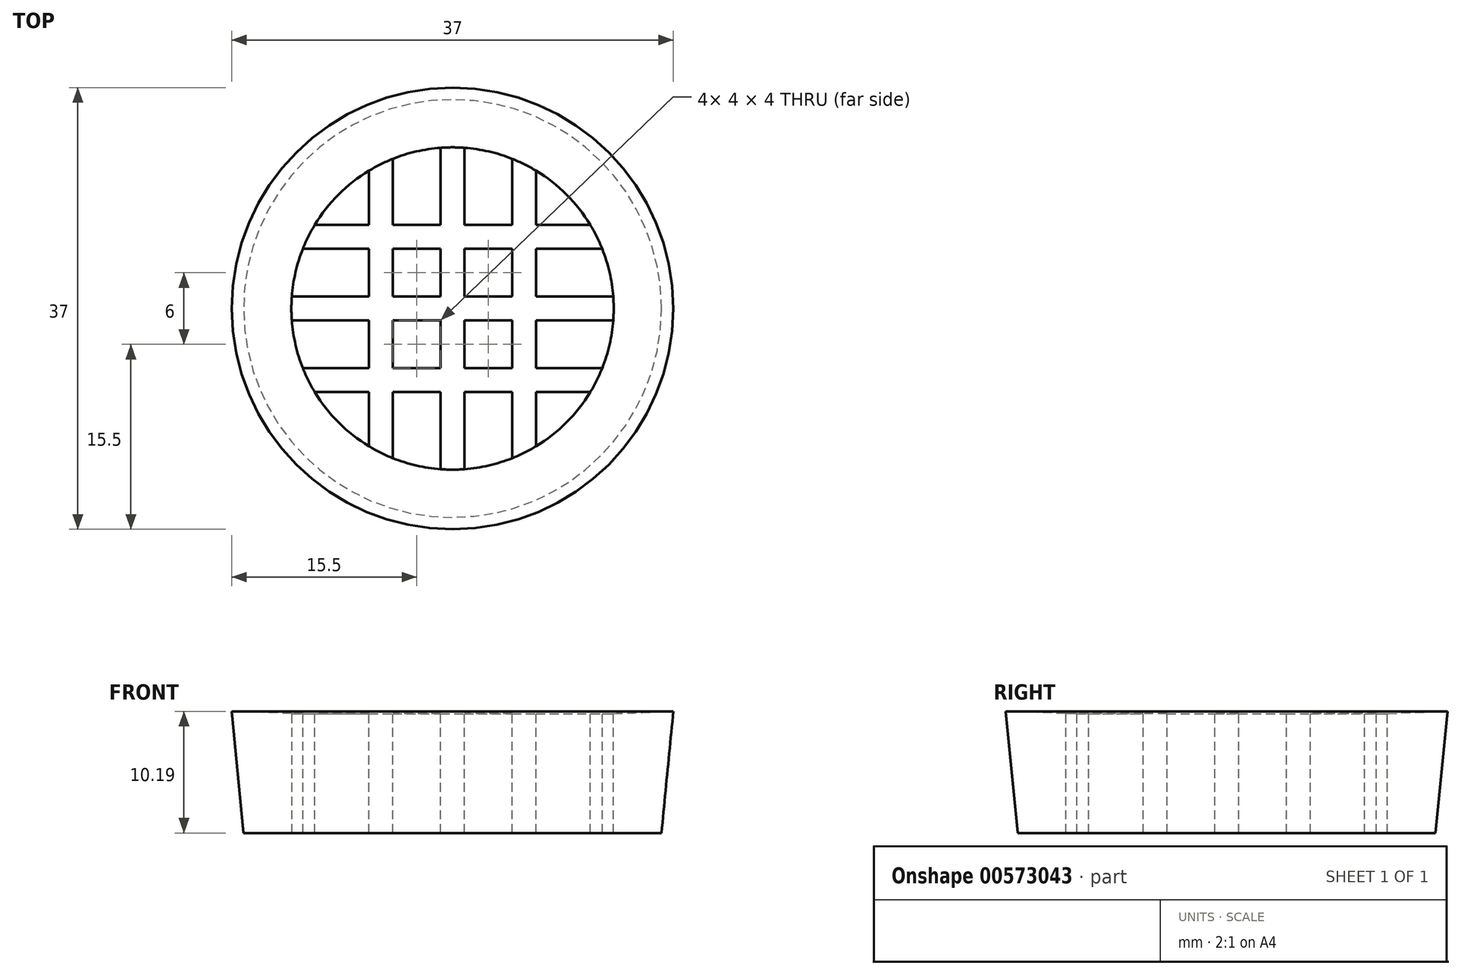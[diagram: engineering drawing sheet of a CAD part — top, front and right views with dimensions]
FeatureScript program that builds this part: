
annotation { "Feature Type Name" : "Feature", "Feature Type Description" : "" }
export const myFeature = defineFeature(function(context is Context, id is Id, definition is map)
    precondition{}
    {
        {
            var Q0;
            Q0=qCreatedBy(makeId("Front.planeOp"),FACE);
            var sketch = newSketch(context, id + "F0", { "sketchPlane" : qUnion([Q0])});
            skLineSegment(sketch, "E0", {"start": v(0, 68.06) * mm, "end": v(0, -62.01) * mm, "construction": true});
            skLineSegment(sketch, "E1", {"start": v(-17.5, 0) * mm, "end": v(-18.5, 10.2) * mm});
            skLineSegment(sketch, "E2", {"start": v(-18.5, 10.2) * mm, "end": v(-13.5, 10) * mm});
            skLineSegment(sketch, "E3", {"start": v(-13.5, 10) * mm, "end": v(-13.5, 0) * mm});
            skLineSegment(sketch, "E4", {"start": v(-13.5, 0) * mm, "end": v(-17.5, 0) * mm});
            skSolve(sketch);
        }
        {
            var Q0;
            Q0=makeQuery(id+"F0.imprint","IMPRINT",FACE,{"disambiguationData":[TD([[makeQuery(id+"F0.imprint","IMPRINT",EDGE,{"derivedFrom":sQuery(id+"F0.wireOp",EDGE,"E1")}),-1.0]])]});
            var Q1;
            Q1=sQuery(id+"F0.wireOp",EDGE,"E0");
            revolve(context, id + "F1", {"surfaceOperationType" : NewSurfaceOperationType.NEW, "entities" : qUnion([Q0]), "axis" : qUnion([Q1]), "revolveType" : RevolveType.FULL});
        }
        {
            var Q0;
            Q0=qCreatedBy(makeId("Top.planeOp"),FACE);
            var sketch = newSketch(context, id + "F2", { "sketchPlane" : qUnion([Q0])});
            skArc(sketch, "E5", {"start": v(-11.67, 7) * mm, "mid": v(-12.2, 6.02) * mm, "end": v(-12.65, 5) * mm});
            skLineSegment(sketch, "E6", {"start": v(-13.57, 1) * mm, "end": v(-7, 1) * mm});
            skLineSegment(sketch, "E7", {"start": v(-13.57, -1) * mm, "end": v(-7, -1) * mm});
            skLineSegment(sketch, "E8", {"start": v(-12.65, 5) * mm, "end": v(-7, 5) * mm});
            skLineSegment(sketch, "E9", {"start": v(-11.67, 7) * mm, "end": v(-7, 7) * mm});
            skLineSegment(sketch, "E10", {"start": v(-12.65, -5) * mm, "end": v(-7, -5) * mm});
            skLineSegment(sketch, "E11", {"start": v(-11.67, -7) * mm, "end": v(-7, -7) * mm});
            skLineSegment(sketch, "E12", {"start": v(15.82, 0) * mm, "end": v(13.6, 0) * mm, "construction": true});
            skLineSegment(sketch, "E13", {"start": v(-1, 13.57) * mm, "end": v(-1, 7) * mm});
            skLineSegment(sketch, "E14", {"start": v(1, -13.57) * mm, "end": v(1, -7) * mm});
            skLineSegment(sketch, "E15", {"start": v(5, 12.65) * mm, "end": v(5, 7) * mm});
            skLineSegment(sketch, "E16", {"start": v(7, -11.67) * mm, "end": v(7, -7) * mm});
            skLineSegment(sketch, "E17", {"start": v(-7, 11.67) * mm, "end": v(-7, 7) * mm});
            skLineSegment(sketch, "E18", {"start": v(-5, -12.65) * mm, "end": v(-5, -7) * mm});
            skLineSegment(sketch, "E19.trimOffspring", {"start": v(-5, 7) * mm, "end": v(-1, 7) * mm});
            skLineSegment(sketch, "E20.trimOffspring", {"start": v(-5, 5) * mm, "end": v(-1, 5) * mm});
            skLineSegment(sketch, "E21.trimOffspring", {"start": v(-7, 5) * mm, "end": v(-7, 1) * mm});
            skLineSegment(sketch, "E22.trimOffspring", {"start": v(-5, 7) * mm, "end": v(-5, 12.65) * mm});
            skLineSegment(sketch, "E23.trimOffspring", {"start": v(-1, 5) * mm, "end": v(-1, 1) * mm});
            skLineSegment(sketch, "E24.trimOffspring", {"start": v(1, 7) * mm, "end": v(5, 7) * mm});
            skLineSegment(sketch, "E25.trimOffspring", {"start": v(7, 7) * mm, "end": v(11.67, 7) * mm});
            skLineSegment(sketch, "E26.trimOffspring", {"start": v(1, 5) * mm, "end": v(5, 5) * mm});
            skLineSegment(sketch, "E27.trimOffspring", {"start": v(1, 1) * mm, "end": v(5, 1) * mm});
            skLineSegment(sketch, "E28.trimOffspring", {"start": v(1, -1) * mm, "end": v(5, -1) * mm});
            skLineSegment(sketch, "E29.trimOffspring", {"start": v(1, -5) * mm, "end": v(5, -5) * mm});
            skLineSegment(sketch, "E30.trimOffspring", {"start": v(1, -7) * mm, "end": v(5, -7) * mm});
            skLineSegment(sketch, "E31.trimOffspring", {"start": v(-1, -7) * mm, "end": v(-1, -13.57) * mm});
            skLineSegment(sketch, "E32.trimOffspring", {"start": v(1, -5) * mm, "end": v(1, -1) * mm});
            skLineSegment(sketch, "E33.trimOffspring", {"start": v(-5, -5) * mm, "end": v(-5, -1) * mm});
            skLineSegment(sketch, "E34.trimOffspring", {"start": v(-7, -7) * mm, "end": v(-7, -11.67) * mm});
            skLineSegment(sketch, "E35.trimOffspring", {"start": v(-5, -5) * mm, "end": v(-1, -5) * mm});
            skLineSegment(sketch, "E36.trimOffspring", {"start": v(-5, -7) * mm, "end": v(-1, -7) * mm});
            skLineSegment(sketch, "E37.trimOffspring", {"start": v(5, 5) * mm, "end": v(5, 1) * mm});
            skLineSegment(sketch, "E38.trimOffspring", {"start": v(7, 5) * mm, "end": v(12.65, 5) * mm});
            skLineSegment(sketch, "E39.trimOffspring", {"start": v(7, 7) * mm, "end": v(7, 11.67) * mm});
            skLineSegment(sketch, "E40.trimOffspring", {"start": v(1, 7) * mm, "end": v(1, 13.57) * mm});
            skLineSegment(sketch, "E41.trimOffspring", {"start": v(7, 1) * mm, "end": v(13.57, 1) * mm});
            skLineSegment(sketch, "E42.trimOffspring", {"start": v(7, 1) * mm, "end": v(7, 5) * mm});
            skLineSegment(sketch, "E43.trimOffspring", {"start": v(1, 0) * mm, "end": v(-1, 0) * mm, "construction": true});
            skLineSegment(sketch, "E44.trimOffspring", {"start": v(7, -1) * mm, "end": v(13.57, -1) * mm});
            skLineSegment(sketch, "E45.trimOffspring", {"start": v(5, -1) * mm, "end": v(5, -5) * mm});
            skLineSegment(sketch, "E46.trimOffspring", {"start": v(7, -5) * mm, "end": v(12.65, -5) * mm});
            skLineSegment(sketch, "E47.trimOffspring", {"start": v(7, -7) * mm, "end": v(11.67, -7) * mm});
            skLineSegment(sketch, "E48.trimOffspring", {"start": v(5, -7) * mm, "end": v(5, -12.65) * mm});
            skLineSegment(sketch, "E49.trimOffspring", {"start": v(7, -5) * mm, "end": v(7, -1) * mm});
            skLineSegment(sketch, "E50.trimOffspring", {"start": v(-5, 0) * mm, "end": v(-30.47, 0) * mm, "construction": true});
            skLineSegment(sketch, "E51.trimOffspring", {"start": v(-5, 1) * mm, "end": v(-5, 5) * mm});
            skLineSegment(sketch, "E52.trimOffspring", {"start": v(-5, -1) * mm, "end": v(-1, -1) * mm});
            skLineSegment(sketch, "E53.trimOffspring", {"start": v(-5, 1) * mm, "end": v(-1, 1) * mm});
            skLineSegment(sketch, "E54.trimOffspring", {"start": v(-7, -1) * mm, "end": v(-7, -5) * mm});
            skLineSegment(sketch, "E55.trimOffspring", {"start": v(-1, -1) * mm, "end": v(-1, -5) * mm});
            skLineSegment(sketch, "E56.trimOffspring", {"start": v(1, 1) * mm, "end": v(1, 5) * mm});
            skArc(sketch, "E57.trimOffspring", {"start": v(-5, 12.65) * mm, "mid": v(-6.02, 12.2) * mm, "end": v(-7, 11.67) * mm});
            skArc(sketch, "E58.trimOffspring", {"start": v(1, 13.57) * mm, "mid": v(0, 13.6) * mm, "end": v(-1, 13.57) * mm});
            skArc(sketch, "E59.trimOffspring", {"start": v(7, 11.67) * mm, "mid": v(6.02, 12.2) * mm, "end": v(5, 12.65) * mm});
            skArc(sketch, "E60.trimOffspring", {"start": v(12.65, 5) * mm, "mid": v(12.2, 6.02) * mm, "end": v(11.67, 7) * mm});
            skArc(sketch, "E61.trimOffspring", {"start": v(13.57, -1) * mm, "mid": v(13.6, 0) * mm, "end": v(13.57, 1) * mm});
            skArc(sketch, "E62.trimOffspring", {"start": v(11.67, -7) * mm, "mid": v(12.2, -6.02) * mm, "end": v(12.65, -5) * mm});
            skArc(sketch, "E63.trimOffspring", {"start": v(5, -12.65) * mm, "mid": v(6.02, -12.2) * mm, "end": v(7, -11.67) * mm});
            skArc(sketch, "E64.trimOffspring", {"start": v(-1, -13.57) * mm, "mid": v(0, -13.6) * mm, "end": v(1, -13.57) * mm});
            skArc(sketch, "E65.trimOffspring", {"start": v(-7, -11.67) * mm, "mid": v(-6.02, -12.2) * mm, "end": v(-5, -12.65) * mm});
            skArc(sketch, "E66.trimOffspring", {"start": v(-12.65, -5) * mm, "mid": v(-12.2, -6.02) * mm, "end": v(-11.67, -7) * mm});
            skArc(sketch, "E67.trimOffspring", {"start": v(-13.57, 1) * mm, "mid": v(-13.6, 0) * mm, "end": v(-13.57, -1) * mm});
            skSolve(sketch);
        }
        {
            var Q0;
            Q0=makeQuery(id+"F2.imprint","IMPRINT",FACE,{"disambiguationData":[TD([[makeQuery(id+"F2.imprint","IMPRINT",EDGE,{"derivedFrom":sQuery(id+"F2.wireOp",EDGE,"E5")}),1.0]])]});
            extrude(context, id + "F3", {"entities" : qUnion([Q0]), "operationType" : NewBodyOperationType.ADD, "depth" : 10 * mm, "offsetDistance" : 25 * mm});
        }
    });
